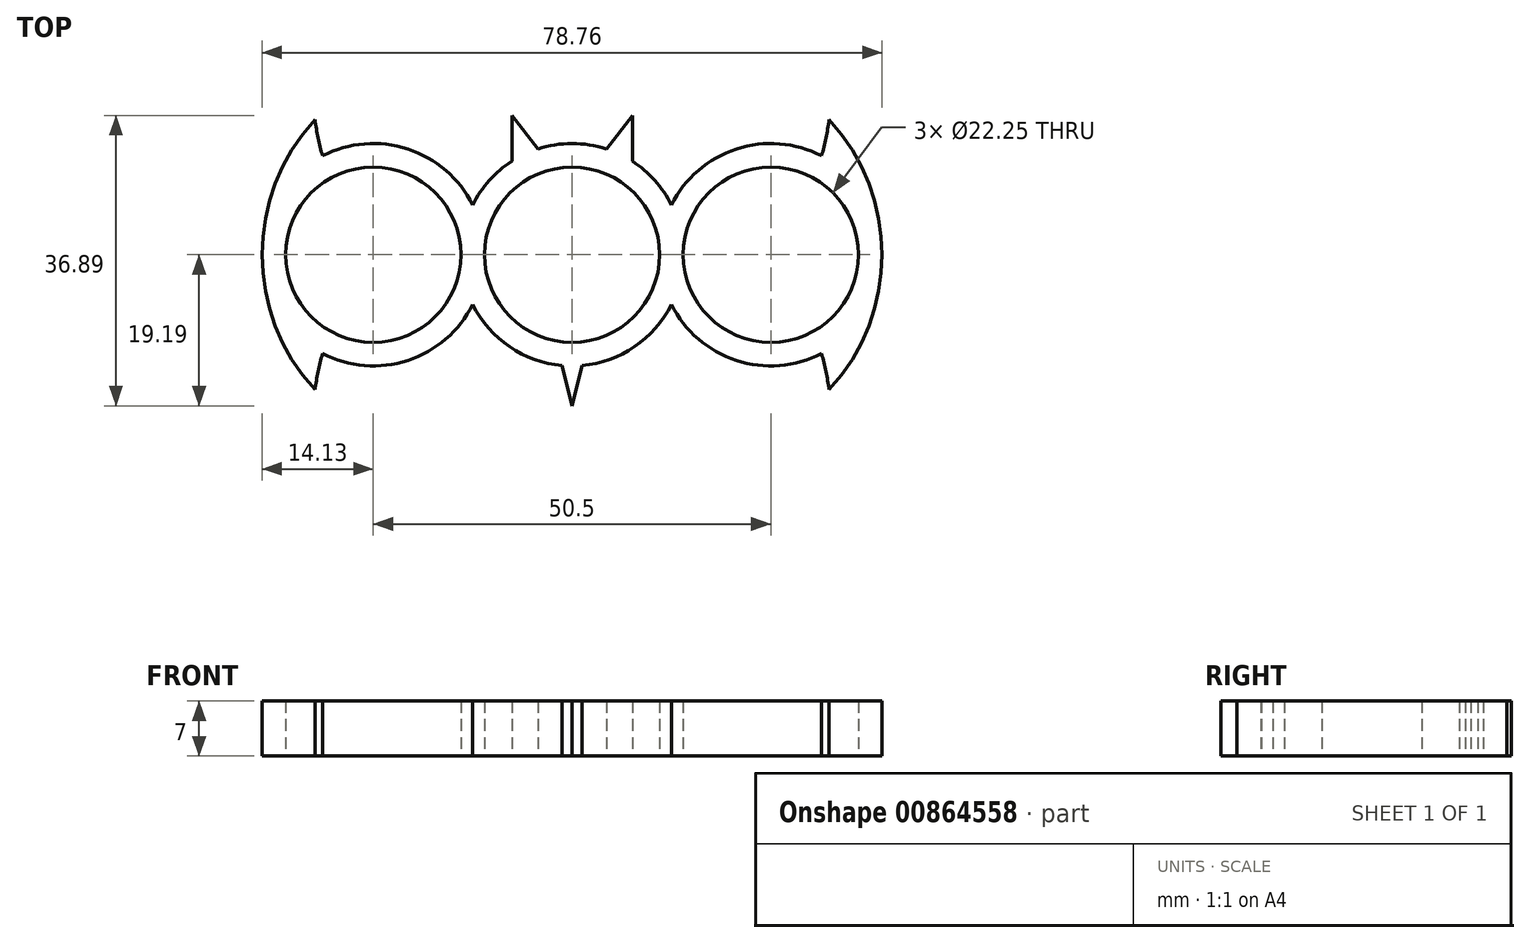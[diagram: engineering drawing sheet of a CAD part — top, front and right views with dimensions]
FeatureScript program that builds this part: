
annotation { "Feature Type Name" : "Feature", "Feature Type Description" : "" }
export const myFeature = defineFeature(function(context is Context, id is Id, definition is map)
    precondition{}
    {
        {
            var Q0;
            Q0=qCreatedBy(makeId("Top.planeOp"),FACE);
            var sketch = newSketch(context, id + "F0", { "sketchPlane" : qUnion([Q0])});
            skCircle(sketch, "E0", {"center": v(0, 0) * mm, "radius": 11.12 * mm});
            skCircle(sketch, "E1", {"center": v(-25.25, 0) * mm, "radius": 11.12 * mm});
            skArc(sketch, "E2", {"start": v(-32.67, 17.14) * mm, "mid": v(-39.38, 0) * mm, "end": v(-32.67, -17.14) * mm});
            skArc(sketch, "E3", {"start": v(-32.67, 17.14) * mm, "mid": v(-32.26, 14.84) * mm, "end": v(-31.7, 12.57) * mm});
            skArc(sketch, "E4.MirrorCS", {"start": v(-32.67, -17.14) * mm, "mid": v(-32.26, -14.84) * mm, "end": v(-31.7, -12.57) * mm});
            skArc(sketch, "E5.0", {"start": v(-31.7, -12.57) * mm, "mid": v(-20.86, -13.43) * mm, "end": v(-12.62, -6.33) * mm});
            skArc(sketch, "E6.trimOffspring", {"start": v(-12.62, 6.33) * mm, "mid": v(-20.86, 13.43) * mm, "end": v(-31.7, 12.57) * mm});
            skArc(sketch, "E7.MirrorCS", {"start": v(32.67, 17.14) * mm, "mid": v(32.26, 14.84) * mm, "end": v(31.7, 12.57) * mm});
            skCircle(sketch, "E8.MirrorC", {"center": v(25.25, 0) * mm, "radius": 11.12 * mm});
            skArc(sketch, "E9.MirrorCS", {"start": v(12.62, 6.33) * mm, "mid": v(20.86, 13.43) * mm, "end": v(31.7, 12.57) * mm});
            skArc(sketch, "E10.MirrorCS", {"start": v(32.67, 17.14) * mm, "mid": v(39.38, 0) * mm, "end": v(32.67, -17.14) * mm});
            skArc(sketch, "E11.MirrorCS", {"start": v(32.67, -17.14) * mm, "mid": v(32.26, -14.84) * mm, "end": v(31.7, -12.57) * mm});
            skArc(sketch, "E12.MirrorCS", {"start": v(31.7, -12.57) * mm, "mid": v(20.86, -13.43) * mm, "end": v(12.62, -6.33) * mm});
            skArc(sketch, "E13", {"start": v(-12.63, 6.33) * mm, "mid": v(-10.5, 9.44) * mm, "end": v(-7.65, 11.87) * mm});
            skArc(sketch, "E14", {"start": v(-12.62, -6.33) * mm, "mid": v(-7.95, -11.68) * mm, "end": v(-1.26, -14.07) * mm});
            skLineSegment(sketch, "E15", {"start": v(4.35, 13.44) * mm, "end": v(7.65, 17.7) * mm});
            skLineSegment(sketch, "E16", {"start": v(7.65, 17.7) * mm, "end": v(7.65, 11.87) * mm});
            skLineSegment(sketch, "E17.MirrorCS", {"start": v(-7.65, 17.7) * mm, "end": v(-7.65, 11.87) * mm});
            skLineSegment(sketch, "E18.MirrorCS", {"start": v(-4.35, 13.44) * mm, "end": v(-7.65, 17.7) * mm});
            skArc(sketch, "E19.trimOffspring", {"start": v(-4.35, 13.44) * mm, "mid": v(0, 14.12) * mm, "end": v(4.35, 13.44) * mm});
            skArc(sketch, "E20.trimOffspring", {"start": v(7.65, 11.87) * mm, "mid": v(10.5, 9.44) * mm, "end": v(12.62, 6.33) * mm});
            skLineSegment(sketch, "E21.trimOffspring", {"start": v(1.26, -14.07) * mm, "end": v(0, -19.2) * mm});
            skLineSegment(sketch, "E22.MirrorCS", {"start": v(-1.26, -14.07) * mm, "end": v(0, -19.2) * mm});
            skArc(sketch, "E23.trimOffspring", {"start": v(1.26, -14.07) * mm, "mid": v(7.95, -11.68) * mm, "end": v(12.62, -6.33) * mm});
            skSolve(sketch);
        }
        {
            var Q0;
            Q0 = qSketchRegion(id + "F0", true);
            extrude(context, id + "F1", {"entities" : qUnion([Q0]), "depth" : 7 * mm, "offsetDistance" : 25 * mm});
        }
    });
